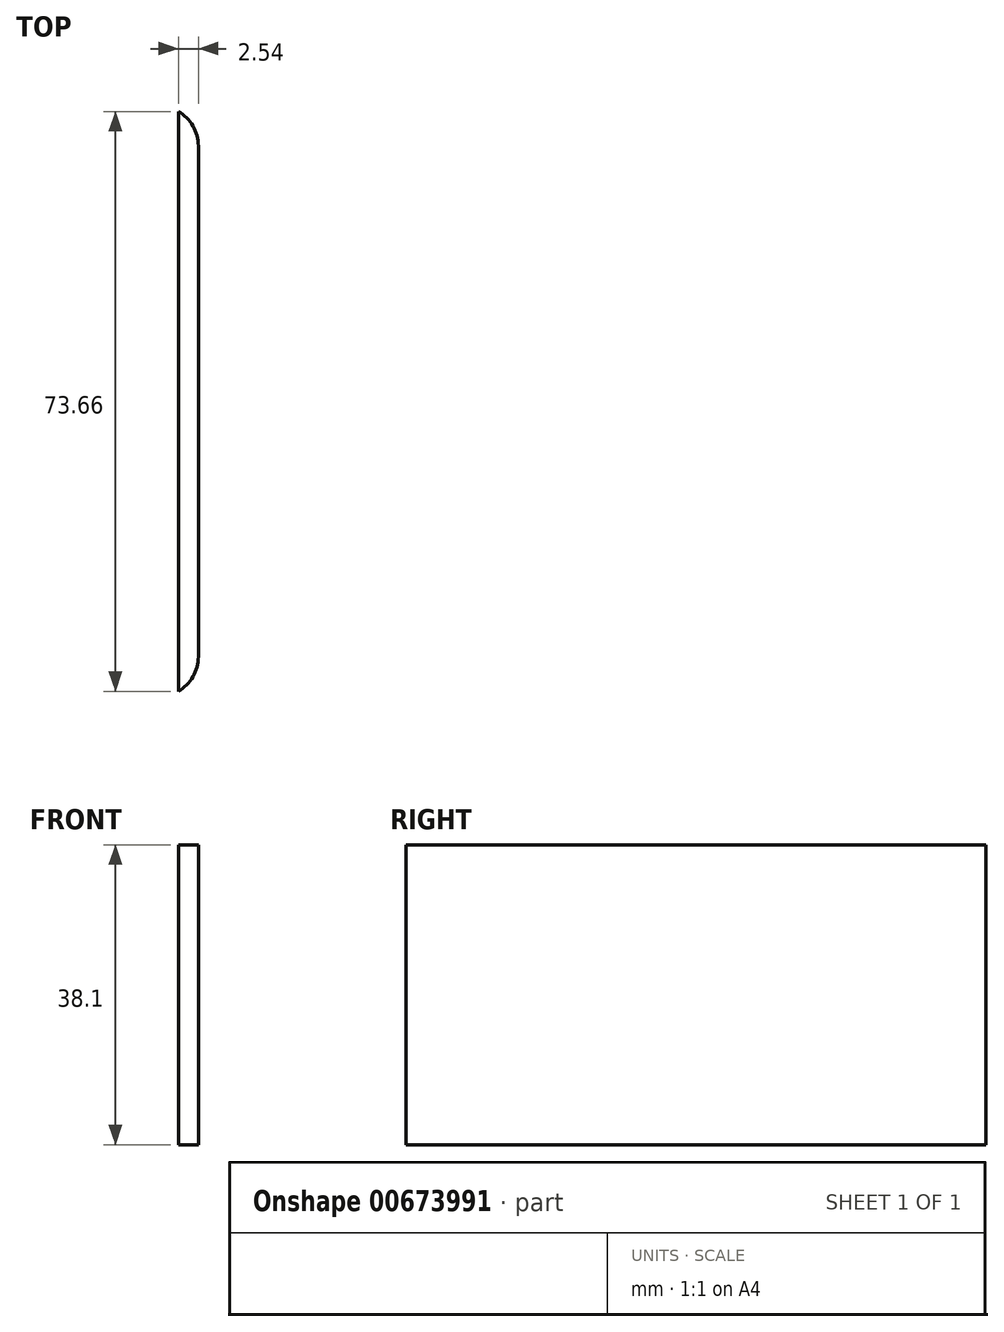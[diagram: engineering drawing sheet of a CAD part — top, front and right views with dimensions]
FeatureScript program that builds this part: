
annotation { "Feature Type Name" : "Feature", "Feature Type Description" : "" }
export const myFeature = defineFeature(function(context is Context, id is Id, definition is map)
    precondition{}
    {
        {
            var Q0;
            Q0=qCreatedBy(makeId("Front.planeOp"),FACE);
            var sketch = newSketch(context, id + "F0", { "sketchPlane" : qUnion([Q0])});
            skLineSegment(sketch, "E0", {"start": v(0, 0) * mm, "end": v(0, 38.1) * mm});
            skLineSegment(sketch, "E1", {"start": v(0, 38.1) * mm, "end": v(2.54, 38.1) * mm});
            skLineSegment(sketch, "E2", {"start": v(2.54, 38.1) * mm, "end": v(2.54, 0) * mm});
            skLineSegment(sketch, "E3", {"start": v(2.54, 0) * mm, "end": v(0, 0) * mm});
            skSolve(sketch);
        }
        {
            var Q0;
            Q0=makeQuery(id+"F0.imprint","IMPRINT",FACE,{"disambiguationData":[TD([[makeQuery(id+"F0.imprint","IMPRINT",EDGE,{"derivedFrom":sQuery(id+"F0.wireOp",EDGE,"E0")}),-1.0]])]});
            extrude(context, id + "F1", {"entities" : qUnion([Q0]), "depth" : 73.66 * mm, "offsetDistance" : 25.4 * mm});
        }
        {
            var Q0;
            Q0=makeQuery(id+"F1.opExtrude","CAP_EDGE",EDGE,{"disambiguationData":[OSD([sQuery(id+"F0.wireOp",EDGE,"E2")])],"isStart":false});
            var Q1;
            Q1=makeQuery(id+"F1.opExtrude","CAP_EDGE",EDGE,{"disambiguationData":[OSD([sQuery(id+"F0.wireOp",EDGE,"E2")])],"isStart":true});
            fillet(context, id + "F2", {"entities" : qUnion([Q0, Q1]), "radius" : 5.08 * mm, "tangentPropagation" : true, "allowEdgeOverflow" : false});
        }
    });
